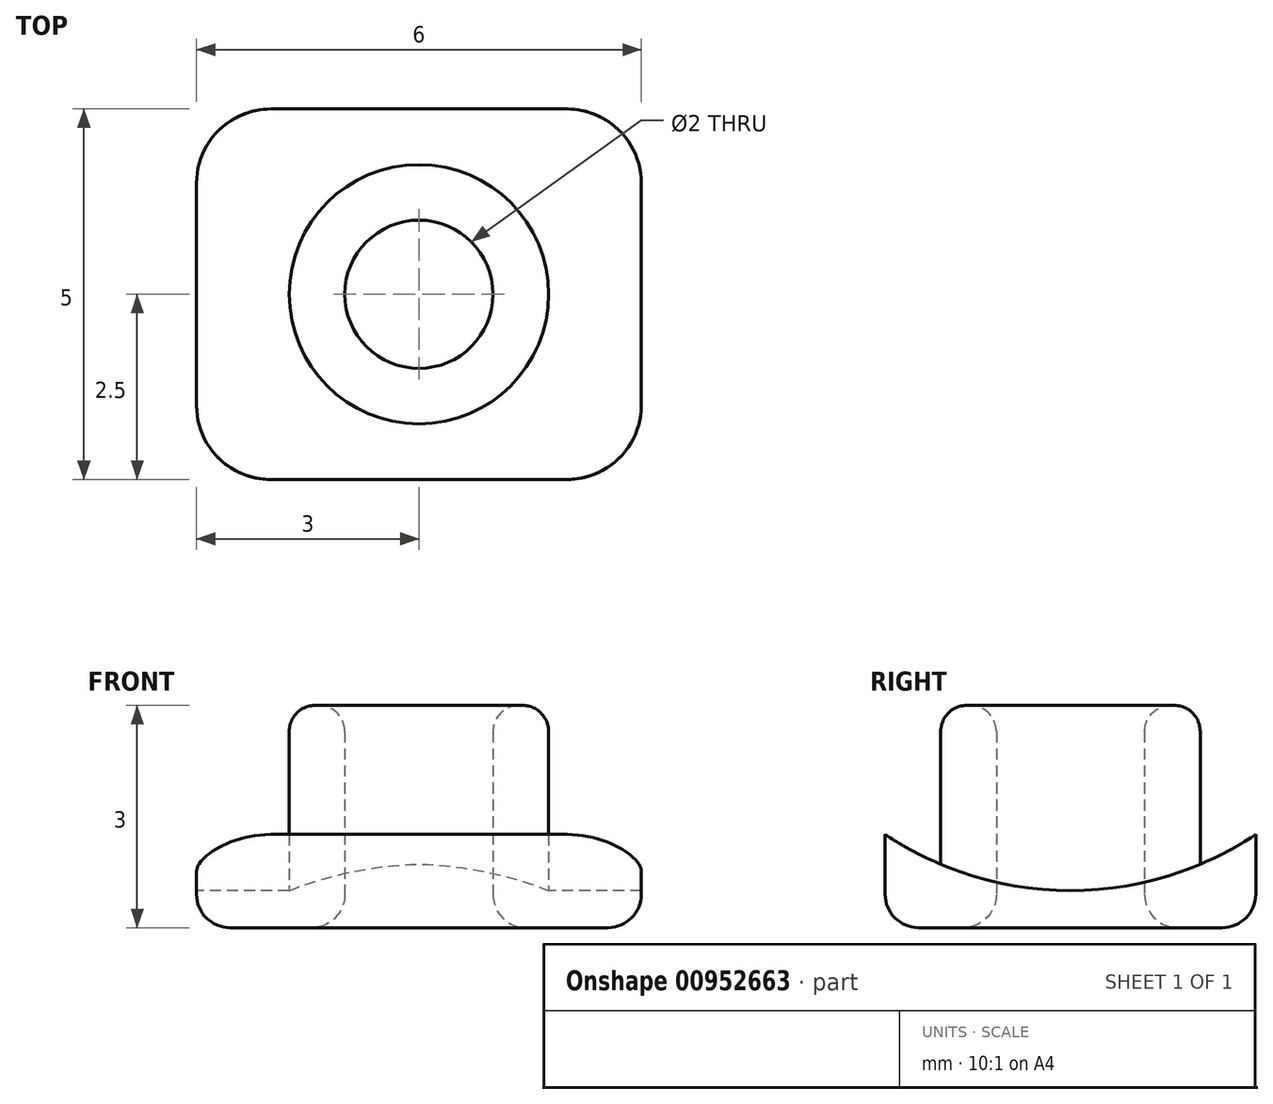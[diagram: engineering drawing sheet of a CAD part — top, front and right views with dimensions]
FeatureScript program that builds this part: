
annotation { "Feature Type Name" : "Feature", "Feature Type Description" : "" }
export const myFeature = defineFeature(function(context is Context, id is Id, definition is map)
    precondition{}
    {
        {
            var Q0;
            Q0=qCreatedBy(makeId("Top.planeOp"),FACE);
            var sketch = newSketch(context, id + "F0", { "sketchPlane" : qUnion([Q0])});
            skCircle(sketch, "E0", {"center": v(0, 0) * mm, "radius": 1 * mm});
            skLineSegment(sketch, "E1.bottom", {"start": v(-2, 2.5) * mm, "end": v(2, 2.5) * mm});
            skLineSegment(sketch, "E1.top", {"start": v(-2, -2.5) * mm, "end": v(2, -2.5) * mm});
            skLineSegment(sketch, "E1.left", {"start": v(-3, 1.5) * mm, "end": v(-3, -1.5) * mm});
            skLineSegment(sketch, "E1.right", {"start": v(3, 1.5) * mm, "end": v(3, -1.5) * mm});
            skPoint(sketch, "E2.visualSharp", {"position": v(-3, 2.5) * mm});
            skArc(sketch, "E2.filletArc", {"start": v(-2, 2.5) * mm, "mid": v(-2.7, 2.2) * mm, "end": v(-3, 1.5) * mm});
            skPoint(sketch, "E3.visualSharp", {"position": v(3, 2.5) * mm});
            skArc(sketch, "E3.filletArc", {"start": v(3, 1.5) * mm, "mid": v(2.7, 2.2) * mm, "end": v(2, 2.5) * mm});
            skPoint(sketch, "E4.visualSharp", {"position": v(3, -2.5) * mm});
            skArc(sketch, "E4.filletArc", {"start": v(2, -2.5) * mm, "mid": v(2.7, -2.2) * mm, "end": v(3, -1.5) * mm});
            skPoint(sketch, "E5.visualSharp", {"position": v(-3, -2.5) * mm});
            skArc(sketch, "E5.filletArc", {"start": v(-3, -1.5) * mm, "mid": v(-2.7, -2.2) * mm, "end": v(-2, -2.5) * mm});
            skCircle(sketch, "E6", {"center": v(0, 0) * mm, "radius": 1.75 * mm});
            skSolve(sketch);
        }
        {
            var Q0;
            Q0=makeQuery(id+"F0.imprint","IMPRINT",FACE,{"disambiguationData":[TD([[makeQuery(id+"F0.imprint","IMPRINT",EDGE,{"derivedFrom":sQuery(id+"F0.wireOp",EDGE,"E1.bottom")}),-1.0]])]});
            extrude(context, id + "F1", {"entities" : qUnion([Q0]), "depth" : 3 * mm, "offsetDistance" : 25 * mm});
        }
        {
            var Q0;
            Q0=qCreatedBy(makeId("Right.planeOp"),FACE);
            var sketch = newSketch(context, id + "F2", { "sketchPlane" : qUnion([Q0])});
            skCircle(sketch, "E7", {"center": v(0, 5) * mm, "radius": 4.5 * mm});
            skSolve(sketch);
        }
        {
            var Q0;
            Q0=makeQuery(id+"F2.imprint","IMPRINT",FACE,{"disambiguationData":[TD([[makeQuery(id+"F2.imprint","IMPRINT",EDGE,{"derivedFrom":sQuery(id+"F2.wireOp",EDGE,"E7")}),1.0]])]});
            extrude(context, id + "F3", {"entities" : qUnion([Q0]), "operationType" : NewBodyOperationType.REMOVE, "endBound" : BoundingType.SYMMETRIC, "depth" : 25 * mm, "offsetDistance" : 25 * mm});
        }
        {
            var Q0;
            Q0=qCreatedBy(makeId("Top.planeOp"),FACE);
            var sketch = newSketch(context, id + "F4", { "sketchPlane" : qUnion([Q0])});
            skCircle(sketch, "E8", {"center": v(0, 0) * mm, "radius": 1.75 * mm});
            skCircle(sketch, "E9", {"center": v(0, 0) * mm, "radius": 1 * mm});
            skSolve(sketch);
        }
        {
            var Q0;
            Q0=makeQuery(id+"F4.imprint","IMPRINT",FACE,{"disambiguationData":[TD([[makeQuery(id+"F4.imprint","IMPRINT",EDGE,{"derivedFrom":sQuery(id+"F4.wireOp",EDGE,"E8")}),1.0]])]});
            extrude(context, id + "F5", {"entities" : qUnion([Q0]), "operationType" : NewBodyOperationType.ADD, "depth" : 3 * mm, "offsetDistance" : 25 * mm});
        }
        {
            var Q0;
            Q0=makeQuery(id+"F5.opExtrude","CAP_EDGE",EDGE,{"disambiguationData":[OSD([sQuery(id+"F4.wireOp",EDGE,"E8")])],"isStart":false});
            var Q1;
            Q1=makeQuery(id+"F5.opExtrude","CAP_EDGE",EDGE,{"disambiguationData":[OSD([sQuery(id+"F4.wireOp",EDGE,"E9")])],"isStart":false});
            fillet(context, id + "F6", {"entities" : qUnion([Q0, Q1]), "radius" : 0.35 * mm, "tangentPropagation" : true, "allowEdgeOverflow" : false});
        }
        {
            var Q0;
            Q0=makeQuery(id+"F5.opExtrude","CAP_EDGE",EDGE,{"disambiguationData":[OSD([sQuery(id+"F4.wireOp",EDGE,"E9")])],"isStart":true});
            var Q1;
            Q1=makeQuery(id+"F5.boolean.opBoolean","MERGE",FACE,{"derivedFrom":[makeQuery(id+"F1.opExtrude","CAP_FACE",FACE,{"disambiguationData":[OSD([sQuery(id+"F0.wireOp",EDGE,"E1.bottom"),sQuery(id+"F0.wireOp",EDGE,"E1.top"),sQuery(id+"F0.wireOp",EDGE,"E1.left"),sQuery(id+"F0.wireOp",EDGE,"E1.right"),sQuery(id+"F0.wireOp",EDGE,"E2.filletArc"),sQuery(id+"F0.wireOp",EDGE,"E3.filletArc"),sQuery(id+"F0.wireOp",EDGE,"E4.filletArc"),sQuery(id+"F0.wireOp",EDGE,"E5.filletArc"),sQuery(id+"F0.wireOp",EDGE,"E6")])],"isStart":true}),makeQuery(id+"F5.opExtrude","CAP_FACE",FACE,{"disambiguationData":[OSD([sQuery(id+"F4.wireOp",EDGE,"E8"),sQuery(id+"F4.wireOp",EDGE,"E9")])],"isStart":true})]});
            fillet(context, id + "F7", {"entities" : qUnion([Q0, Q1]), "radius" : 0.45 * mm, "tangentPropagation" : true, "allowEdgeOverflow" : false});
        }
    });
